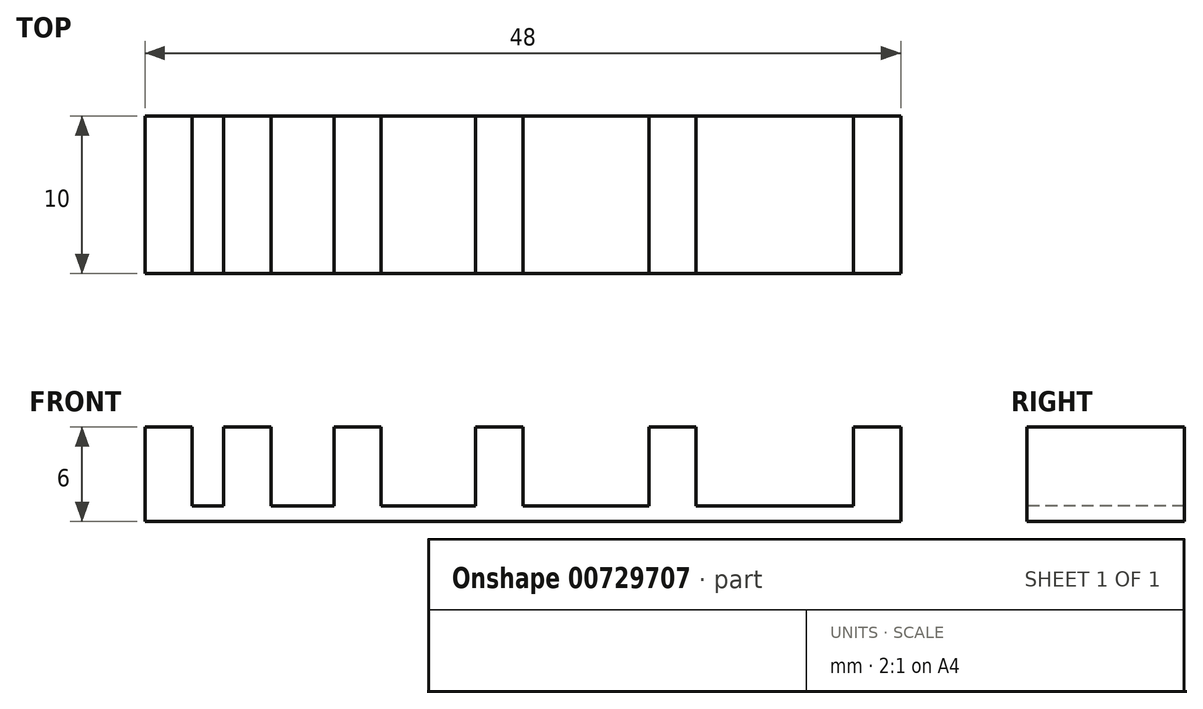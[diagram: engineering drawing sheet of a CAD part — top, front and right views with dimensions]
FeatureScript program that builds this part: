
annotation { "Feature Type Name" : "Feature", "Feature Type Description" : "" }
export const myFeature = defineFeature(function(context is Context, id is Id, definition is map)
    precondition{}
    {
        {
            var Q0;
            Q0=qCreatedBy(makeId("Top.planeOp"),FACE);
            var sketch = newSketch(context, id + "F0", { "sketchPlane" : qUnion([Q0])});
            skLineSegment(sketch, "E0.bottom", {"start": v(-28.46, 0) * mm, "end": v(-25.46, 0) * mm});
            skLineSegment(sketch, "E0.top", {"start": v(-28.46, -10) * mm, "end": v(-25.46, -10) * mm});
            skLineSegment(sketch, "E0.left", {"start": v(-28.46, 0) * mm, "end": v(-28.46, -10) * mm});
            skLineSegment(sketch, "E0.right", {"start": v(-25.46, 0) * mm, "end": v(-25.46, -10) * mm});
            skLineSegment(sketch, "E1.bottom", {"start": v(-23.46, 0) * mm, "end": v(-20.46, 0) * mm});
            skLineSegment(sketch, "E1.top", {"start": v(-23.46, -10) * mm, "end": v(-20.46, -10) * mm});
            skLineSegment(sketch, "E1.left", {"start": v(-23.46, 0) * mm, "end": v(-23.46, -10) * mm});
            skLineSegment(sketch, "E1.right", {"start": v(-20.46, 0) * mm, "end": v(-20.46, -10) * mm});
            skLineSegment(sketch, "E2.bottom", {"start": v(-16.46, 0) * mm, "end": v(-13.46, 0) * mm});
            skLineSegment(sketch, "E2.top", {"start": v(-16.46, -10) * mm, "end": v(-13.46, -10) * mm});
            skLineSegment(sketch, "E2.left", {"start": v(-16.46, 0) * mm, "end": v(-16.46, -10) * mm});
            skLineSegment(sketch, "E2.right", {"start": v(-13.46, 0) * mm, "end": v(-13.46, -10) * mm});
            skLineSegment(sketch, "E3.bottom", {"start": v(-7.46, 0) * mm, "end": v(-4.46, 0) * mm});
            skLineSegment(sketch, "E3.top", {"start": v(-7.46, -10) * mm, "end": v(-4.46, -10) * mm});
            skLineSegment(sketch, "E3.left", {"start": v(-7.46, 0) * mm, "end": v(-7.46, -10) * mm});
            skLineSegment(sketch, "E3.right", {"start": v(-4.46, 0) * mm, "end": v(-4.46, -10) * mm});
            skLineSegment(sketch, "E4.bottom", {"start": v(3.54, 0) * mm, "end": v(6.54, 0) * mm});
            skLineSegment(sketch, "E4.top", {"start": v(3.54, -10) * mm, "end": v(6.54, -10) * mm});
            skLineSegment(sketch, "E4.left", {"start": v(3.54, 0) * mm, "end": v(3.54, -10) * mm});
            skLineSegment(sketch, "E4.right", {"start": v(6.54, 0) * mm, "end": v(6.54, -10) * mm});
            skLineSegment(sketch, "E5.bottom", {"start": v(16.54, 0) * mm, "end": v(19.54, 0) * mm});
            skLineSegment(sketch, "E5.top", {"start": v(16.54, -10) * mm, "end": v(19.54, -10) * mm});
            skLineSegment(sketch, "E5.left", {"start": v(16.54, 0) * mm, "end": v(16.54, -10) * mm});
            skLineSegment(sketch, "E5.right", {"start": v(19.54, 0) * mm, "end": v(19.54, -10) * mm});
            skSolve(sketch);
        }
        {
            var Q0;
            Q0=qSketchRegion(id+"F0",true);
            extrude(context, id + "F1", {"entities" : qUnion([Q0]), "depth" : 5 * mm, "offsetDistance" : 25 * mm});
        }
        {
            var Q0;
            Q0=makeQuery(id+"F1.opExtrude","CAP_FACE",FACE,{"disambiguationData":[OSD([sQuery(id+"F0.wireOp",EDGE,"E0.bottom"),sQuery(id+"F0.wireOp",EDGE,"E0.top"),sQuery(id+"F0.wireOp",EDGE,"E0.left"),sQuery(id+"F0.wireOp",EDGE,"E0.right")])],"isStart":true});
            var sketch = newSketch(context, id + "F2", { "sketchPlane" : qUnion([Q0])});
            skPoint(sketch, "E6.0", {"position": v(19.54, 0) * mm});
            skLineSegment(sketch, "E7.bottom", {"start": v(-28.46, 10) * mm, "end": v(19.54, 10) * mm});
            skLineSegment(sketch, "E7.top", {"start": v(-28.46, 0) * mm, "end": v(19.54, 0) * mm});
            skLineSegment(sketch, "E7.left", {"start": v(-28.46, 10) * mm, "end": v(-28.46, 0) * mm});
            skLineSegment(sketch, "E7.right", {"start": v(19.54, 10) * mm, "end": v(19.54, 0) * mm});
            skSolve(sketch);
        }
        {
            var Q0;
            {var subQ2=sQuery(id+"F2.wireOp",EDGE,"E7.right");Q0=makeQuery(id+"F2.imprint","IMPRINT",FACE,{"disambiguationData":[TD([[makeQuery(id+"F2.imprint","IMPRINT",EDGE,{"derivedFrom":subQ2}),-1.0]])]});}
            var Q1;
            {var subQ0=sQuery(id+"F2.wireOp",EDGE,"E7.left");Q1=makeQuery(id+"F2.imprint","IMPRINT",FACE,{"disambiguationData":[TD([[makeQuery(id+"F2.imprint","IMPRINT",EDGE,{"derivedFrom":subQ0}),-1.0]])]});}
            extrude(context, id + "F3", {"entities" : qUnion([Q0, Q1]), "operationType" : NewBodyOperationType.ADD, "depth" : 1 * mm, "offsetDistance" : 25 * mm});
        }
    });
